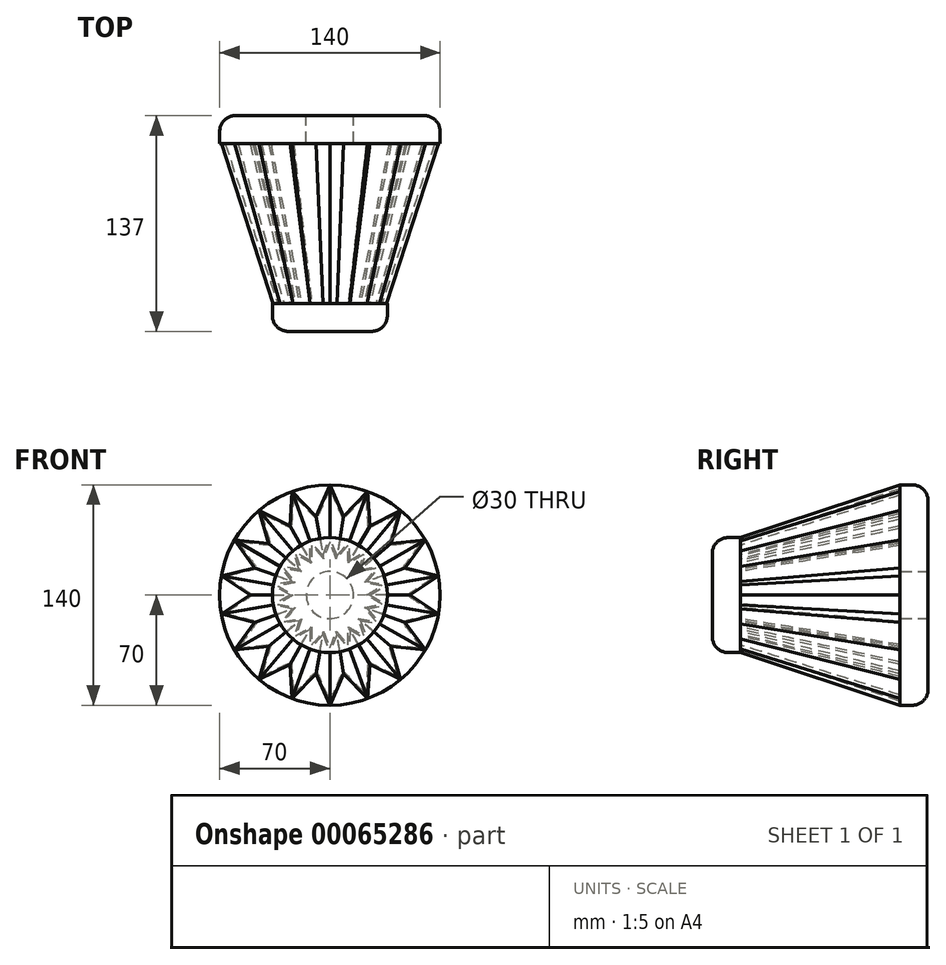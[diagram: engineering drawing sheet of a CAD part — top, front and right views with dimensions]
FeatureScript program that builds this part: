
annotation { "Feature Type Name" : "Feature", "Feature Type Description" : "" }
export const myFeature = defineFeature(function(context is Context, id is Id, definition is map)
    precondition{}
    {
        {
            var Q0;
            Q0=qCreatedBy(makeId("Front.planeOp"),FACE);
            var sketch = newSketch(context, id + "F0", { "sketchPlane" : qUnion([Q0])});
            skLineSegment(sketch, "E0", {"start": v(0, 70) * mm, "end": v(0, 0) * mm, "construction": true});
            skLineSegment(sketch, "E1", {"start": v(0, 70) * mm, "end": v(-8.82, 50) * mm});
            skLineSegment(sketch, "E2", {"start": v(-8.82, 50) * mm, "end": v(0, 0) * mm});
            skLineSegment(sketch, "E3.MirrorCS", {"start": v(0, 70) * mm, "end": v(8.82, 50) * mm});
            skLineSegment(sketch, "E4.MirrorCS", {"start": v(8.82, 50) * mm, "end": v(0, 0) * mm});
            skSolve(sketch);
        }
        {
            var Q0;
            Q0=qCreatedBy(makeId("Front.planeOp"),FACE);
            cPlane(context, id + "F1", {"entities" : qUnion([Q0]), "cplaneType" : CPlaneType.OFFSET, "offset" : 101.5 * mm, "width" : 152.4 * mm, "height" : 152.4 * mm});
        }
        {
            var Q0;
            Q0=qCreatedBy(id+"F1.planeOp",FACE);
            var sketch = newSketch(context, id + "F2", { "sketchPlane" : qUnion([Q0])});
            skLineSegment(sketch, "E5", {"start": v(0, 0) * mm, "end": v(0, 70) * mm, "construction": true});
            skLineSegment(sketch, "E6", {"start": v(0, 0) * mm, "end": v(-4.4, 25) * mm});
            skLineSegment(sketch, "E7", {"start": v(-4.4, 25) * mm, "end": v(0, 36.5) * mm});
            skLineSegment(sketch, "E8.MirrorCS", {"start": v(4.4, 25) * mm, "end": v(0, 36.5) * mm});
            skLineSegment(sketch, "E9.MirrorCS", {"start": v(0, 0) * mm, "end": v(4.4, 25) * mm});
            skSolve(sketch);
        }
        {
            var Q0;
            Q0 = qSketchRegion(id + "F0", true);
            var Q1;
            Q1 = qSketchRegion(id + "F2", true);
            loft(context, id + "F3", {"sheetProfilesArray" : [{ "sheetProfileEntities" : qUnion([Q0]) }, { "sheetProfileEntities" : qUnion([Q1]) }]});
        }
        {
            var Q0;
            Q0=makeQuery(id+"F3.opLoft","SWEPT_BODY",BODY,{"disambiguationData":[OSD([makeQuery(id+"F0.imprint","IMPRINT",FACE,{"disambiguationData":[TD([[makeQuery(id+"F0.imprint","IMPRINT",EDGE,{"derivedFrom":sQuery(id+"F0.wireOp",EDGE,"E1")}),1.0]])]}),makeQuery(id+"F2.imprint","IMPRINT",FACE,{"disambiguationData":[TD([[makeQuery(id+"F2.imprint","IMPRINT",EDGE,{"derivedFrom":sQuery(id+"F2.wireOp",EDGE,"E6")}),-1.0]])]})])]});
            var Q1;
            Q1=makeQuery(id+"F3.opLoft","SWEPT_EDGE",EDGE,{"disambiguationData":[OSD([sQuery(id+"F0.wireOp",EDGE,"E2"),sQuery(id+"F0.wireOp",EDGE,"E4.MirrorCS"),sQuery(id+"F2.wireOp",EDGE,"E6"),sQuery(id+"F2.wireOp",EDGE,"E9.MirrorCS")])]});
            circularPattern(context, id + "F4", {"operationType" : NewBodyOperationType.ADD, "entities" : qUnion([Q0]), "axis" : qUnion([Q1]), "angle" : 360 * degree, "instanceCount" : 18, "equalSpace" : true});
        }
        {
            var Q0;
            {var subQ0=makeQuery(id+"F3.opLoft","CAP_FACE",FACE,{"disambiguationData":[OSD([makeQuery(id+"F0.imprint","IMPRINT",FACE,{"disambiguationData":[TD([[makeQuery(id+"F0.imprint","IMPRINT",EDGE,{"derivedFrom":sQuery(id+"F0.wireOp",EDGE,"E1")}),1.0]])]})])],"isStart":true});Q0=makeQuery(id+"F4.boolean.opBoolean","MERGE",FACE,{"derivedFrom":[subQ0,makeQuery(id+"F4.opPattern","COPY",FACE,{"derivedFrom":subQ0,"instanceName":"1"}),makeQuery(id+"F4.opPattern","COPY",FACE,{"derivedFrom":subQ0,"instanceName":"2"}),makeQuery(id+"F4.opPattern","COPY",FACE,{"derivedFrom":subQ0,"instanceName":"3"}),makeQuery(id+"F4.opPattern","COPY",FACE,{"derivedFrom":subQ0,"instanceName":"4"}),makeQuery(id+"F4.opPattern","COPY",FACE,{"derivedFrom":subQ0,"instanceName":"5"}),makeQuery(id+"F4.opPattern","COPY",FACE,{"derivedFrom":subQ0,"instanceName":"6"}),makeQuery(id+"F4.opPattern","COPY",FACE,{"derivedFrom":subQ0,"instanceName":"7"}),makeQuery(id+"F4.opPattern","COPY",FACE,{"derivedFrom":subQ0,"instanceName":"8"}),makeQuery(id+"F4.opPattern","COPY",FACE,{"derivedFrom":subQ0,"instanceName":"9"}),makeQuery(id+"F4.opPattern","COPY",FACE,{"derivedFrom":subQ0,"instanceName":"10"}),makeQuery(id+"F4.opPattern","COPY",FACE,{"derivedFrom":subQ0,"instanceName":"11"}),makeQuery(id+"F4.opPattern","COPY",FACE,{"derivedFrom":subQ0,"instanceName":"12"}),makeQuery(id+"F4.opPattern","COPY",FACE,{"derivedFrom":subQ0,"instanceName":"13"}),makeQuery(id+"F4.opPattern","COPY",FACE,{"derivedFrom":subQ0,"instanceName":"14"}),makeQuery(id+"F4.opPattern","COPY",FACE,{"derivedFrom":subQ0,"instanceName":"15"}),makeQuery(id+"F4.opPattern","COPY",FACE,{"derivedFrom":subQ0,"instanceName":"16"}),makeQuery(id+"F4.opPattern","COPY",FACE,{"derivedFrom":subQ0,"instanceName":"17"})]});}
            var Q1;
            {var subQ0=makeQuery(id+"F3.opLoft","CAP_FACE",FACE,{"disambiguationData":[OSD([makeQuery(id+"F2.imprint","IMPRINT",FACE,{"disambiguationData":[TD([[makeQuery(id+"F2.imprint","IMPRINT",EDGE,{"derivedFrom":sQuery(id+"F2.wireOp",EDGE,"E6")}),-1.0]])]})])],"isStart":true});Q1=makeQuery(id+"F4.boolean.opBoolean","MERGE",FACE,{"derivedFrom":[subQ0,makeQuery(id+"F4.opPattern","COPY",FACE,{"derivedFrom":subQ0,"instanceName":"1"}),makeQuery(id+"F4.opPattern","COPY",FACE,{"derivedFrom":subQ0,"instanceName":"2"}),makeQuery(id+"F4.opPattern","COPY",FACE,{"derivedFrom":subQ0,"instanceName":"3"}),makeQuery(id+"F4.opPattern","COPY",FACE,{"derivedFrom":subQ0,"instanceName":"4"}),makeQuery(id+"F4.opPattern","COPY",FACE,{"derivedFrom":subQ0,"instanceName":"5"}),makeQuery(id+"F4.opPattern","COPY",FACE,{"derivedFrom":subQ0,"instanceName":"6"}),makeQuery(id+"F4.opPattern","COPY",FACE,{"derivedFrom":subQ0,"instanceName":"7"}),makeQuery(id+"F4.opPattern","COPY",FACE,{"derivedFrom":subQ0,"instanceName":"8"}),makeQuery(id+"F4.opPattern","COPY",FACE,{"derivedFrom":subQ0,"instanceName":"9"}),makeQuery(id+"F4.opPattern","COPY",FACE,{"derivedFrom":subQ0,"instanceName":"10"}),makeQuery(id+"F4.opPattern","COPY",FACE,{"derivedFrom":subQ0,"instanceName":"11"}),makeQuery(id+"F4.opPattern","COPY",FACE,{"derivedFrom":subQ0,"instanceName":"12"}),makeQuery(id+"F4.opPattern","COPY",FACE,{"derivedFrom":subQ0,"instanceName":"13"}),makeQuery(id+"F4.opPattern","COPY",FACE,{"derivedFrom":subQ0,"instanceName":"14"}),makeQuery(id+"F4.opPattern","COPY",FACE,{"derivedFrom":subQ0,"instanceName":"15"}),makeQuery(id+"F4.opPattern","COPY",FACE,{"derivedFrom":subQ0,"instanceName":"16"}),makeQuery(id+"F4.opPattern","COPY",FACE,{"derivedFrom":subQ0,"instanceName":"17"})]});}
            shell(context, id + "F5", {"entities" : qUnion([Q0, Q1]), "thickness" : 1 * mm});
        }
        {
            var Q0;
            Q0=qCreatedBy(makeId("Front.planeOp"),FACE);
            var sketch = newSketch(context, id + "F6", { "sketchPlane" : qUnion([Q0])});
            skCircle(sketch, "E10", {"center": v(0, 0) * mm, "radius": 70 * mm});
            skSolve(sketch);
        }
        {
            var Q0;
            Q0 = qSketchRegion(id + "F6", true);
            extrude(context, id + "F7", {"entities" : qUnion([Q0]), "oppositeDirection" : true, "depth" : 17.75 * mm});
        }
        {
            var Q0;
            Q0=qCreatedBy(id+"F1.planeOp",FACE);
            var sketch = newSketch(context, id + "F8", { "sketchPlane" : qUnion([Q0])});
            skCircle(sketch, "E11", {"center": v(0, 0) * mm, "radius": 36.5 * mm});
            skSolve(sketch);
        }
        {
            var Q0;
            Q0 = qSketchRegion(id + "F8", true);
            extrude(context, id + "F9", {"entities" : qUnion([Q0]), "depth" : 17.75 * mm});
        }
        {
            var Q0;
            Q0=makeQuery(id+"F9.opExtrude","CAP_EDGE",EDGE,{"disambiguationData":[OSD([sQuery(id+"F8.wireOp",EDGE,"E11")])],"isStart":false});
            var Q1;
            Q1=makeQuery(id+"F7.opExtrude","CAP_EDGE",EDGE,{"disambiguationData":[OSD([sQuery(id+"F6.wireOp",EDGE,"E10")])],"isStart":false});
            fillet(context, id + "F10", {"entities" : qUnion([Q0, Q1]), "radius" : 10 * mm, "tangentPropagation" : true, "allowEdgeOverflow" : false});
        }
        {
            var Q0;
            Q0=makeQuery(id+"F7.opExtrude","CAP_FACE",FACE,{"disambiguationData":[OSD([sQuery(id+"F6.wireOp",EDGE,"E10")])],"isStart":false});
            var sketch = newSketch(context, id + "F11", { "sketchPlane" : qUnion([Q0])});
            skCircle(sketch, "E12", {"center": v(0, 0) * mm, "radius": 15 * mm});
            skSolve(sketch);
        }
        {
            var Q0;
            Q0 = qSketchRegion(id + "F11", true);
            extrude(context, id + "F12", {"entities" : qUnion([Q0]), "operationType" : NewBodyOperationType.REMOVE, "oppositeDirection" : true, "depth" : 17.75 * mm});
        }
    });
